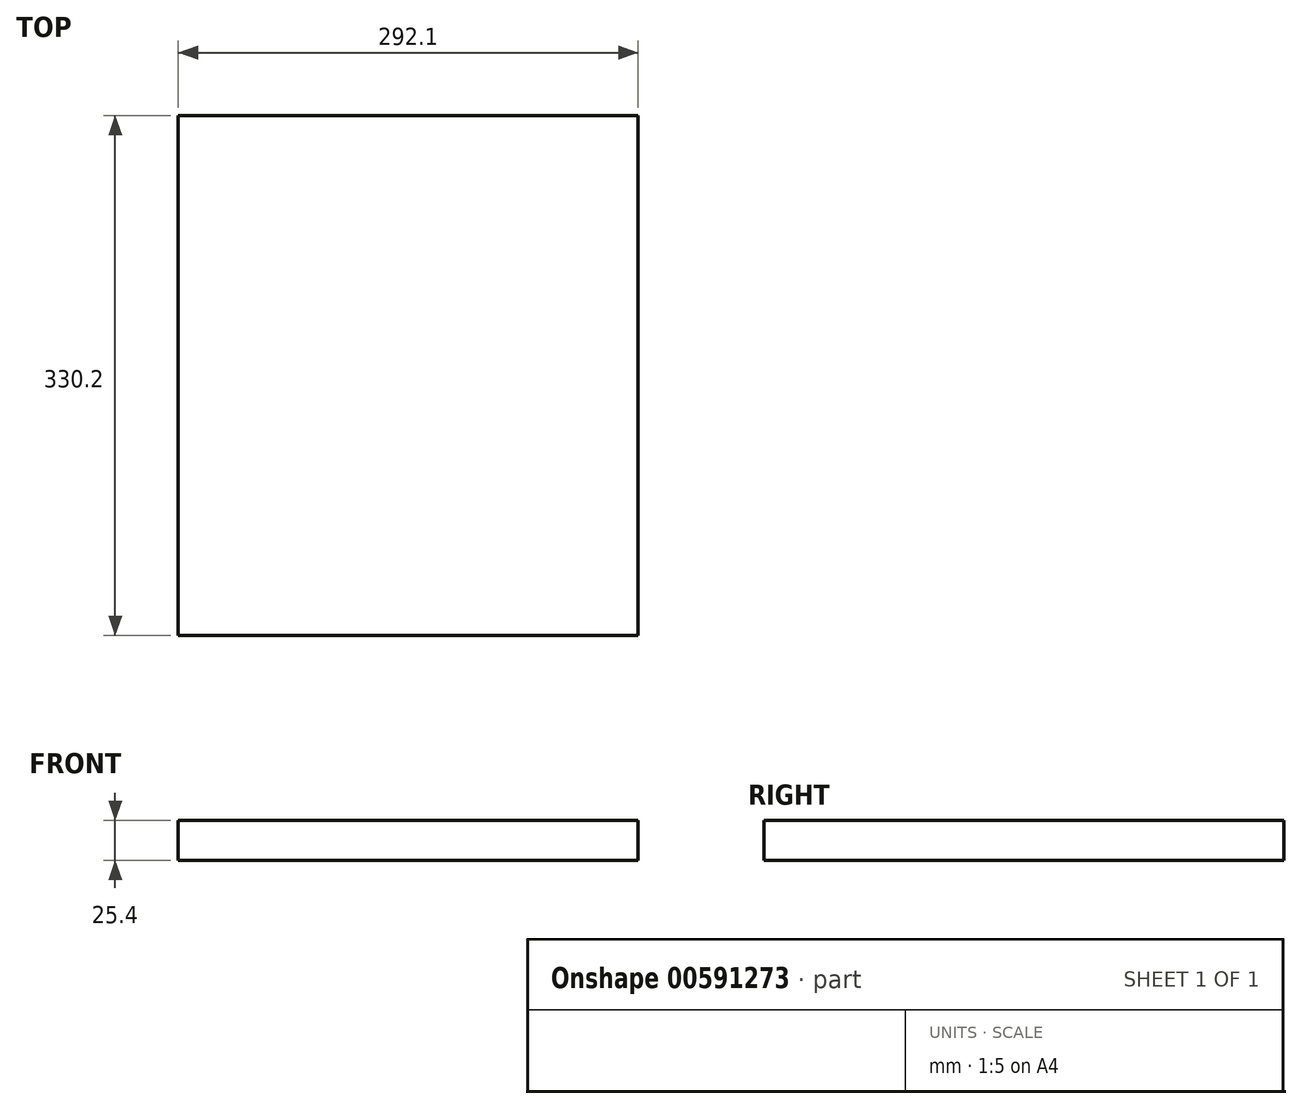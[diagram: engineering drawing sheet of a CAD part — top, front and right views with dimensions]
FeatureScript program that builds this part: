
annotation { "Feature Type Name" : "Feature", "Feature Type Description" : "" }
export const myFeature = defineFeature(function(context is Context, id is Id, definition is map)
    precondition{}
    {
        {
            var Q0;
            Q0=qCreatedBy(makeId("Top.planeOp"),FACE);
            var sketch = newSketch(context, id + "F0", { "sketchPlane" : qUnion([Q0])});
            skLineSegment(sketch, "E0.bottom", {"start": v(146.05, -165.1) * mm, "end": v(-146.05, -165.1) * mm});
            skLineSegment(sketch, "E0.top", {"start": v(146.05, 165.1) * mm, "end": v(-146.05, 165.1) * mm});
            skLineSegment(sketch, "E0.left", {"start": v(146.05, -165.1) * mm, "end": v(146.05, 165.1) * mm});
            skLineSegment(sketch, "E0.right", {"start": v(-146.05, -165.1) * mm, "end": v(-146.05, 165.1) * mm});
            skPoint(sketch, "E0.middle", {"position": v(0, 0) * mm});
            skSolve(sketch);
        }
        {
            var Q0;
            Q0=makeQuery(id+"F0.imprint","IMPRINT",FACE,{"disambiguationData":[TD([[makeQuery(id+"F0.imprint","IMPRINT",EDGE,{"derivedFrom":sQuery(id+"F0.wireOp",EDGE,"E0.bottom")}),-1.0]])]});
            extrude(context, id + "F1", {"entities" : qUnion([Q0]), "depth" : 25.4 * mm, "offsetDistance" : 25.4 * mm});
        }
    });
